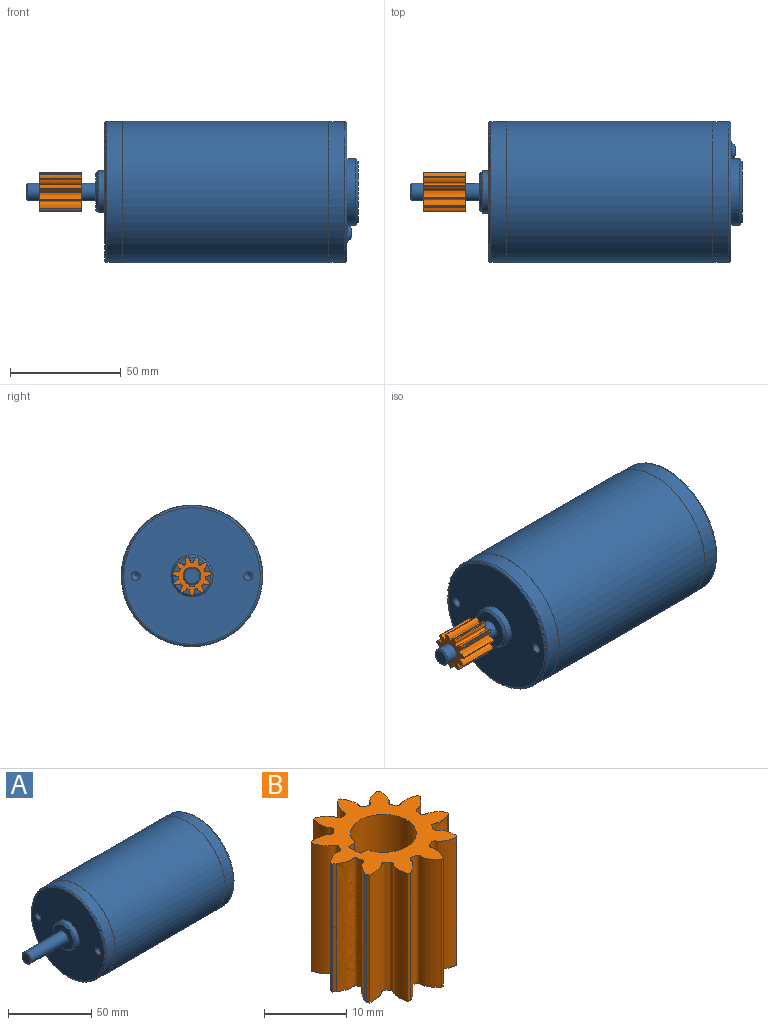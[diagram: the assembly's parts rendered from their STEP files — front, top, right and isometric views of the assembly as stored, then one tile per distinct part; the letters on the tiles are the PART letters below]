
ASSEMBLY  parts=2 mates=1
PART A: 33 faces, bbox 150.2x69x69 mm
  f0: cone r=4mm half-angle=45deg, axis (1,0,0), area 16.7mm2, adj f18,f22
  f1: cone r=9.53mm half-angle=45deg, axis (1,0,0), area 81.4mm2, adj f13,f27
  f2: cone r=14.02mm half-angle=45deg, axis (-1,0,0), area 131.2mm2, adj f17,f23
  f3: cone r=2.12mm half-angle=45deg, axis (-1,0,0), area 62.9mm2, adj f5,f29
  f4: cone r=2.12mm half-angle=45deg, axis (-1,0,0), area 62.9mm2, adj f6,f28
  f5: cylinder r=4.32mm len=8.64mm, axis (-1,0,0), area 1.3mm2, adj f3,f21
  f6: cylinder r=4.32mm len=8.64mm, axis (-1,0,0), area 1.3mm2, adj f4,f21
  f7: cone r=2.02mm half-angle=59deg, axis (-1,0,0), area 14.9mm2, adj f8
  f8: cylinder r=2.02mm len=13.61mm, axis (-1,0,0), area 172.7mm2, adj f7,f26
  f9: cone r=2.02mm half-angle=59deg, axis (-1,0,0), area 14.9mm2, adj f10
  f10: cylinder r=2.02mm len=13.61mm, axis (-1,0,0), area 172.7mm2, adj f9,f26
  f11: torus R=30.88mm, axis (1,0,0), area 311mm2, adj f16,f21
  f12: torus R=30.88mm, axis (-1,0,0), area 311mm2, adj f14,f26
  f13: cylinder r=9.53mm len=19.05mm, axis (1,0,0), area 178.6mm2, adj f1,f26
  f14: cylinder r=31.88mm len=63.75mm, axis (1,0,0), area 1448mm2, adj f12,f25
  f15: cylinder r=32mm len=93.14mm, axis (1,0,0), area 18729.4mm2, adj f24,f25
  f16: cylinder r=31.88mm len=63.75mm, axis (1,0,0), area 1448mm2, adj f11,f24
  f17: cylinder r=15.04mm len=30.07mm, axis (1,0,0), area 376.4mm2, adj f2,f21
  f18: cylinder r=4mm len=31.1mm, axis (1,0,0), area 739mm2, adj f0,f19,f20,f27,f31,f32
  f19: cylinder r=1mm len=2mm, axis (0,1,0), area 3.4mm2, adj f18,f30,f31,f32
  f20: cylinder r=1mm len=2mm, axis (0,-1,0), area 3.4mm2, adj f18,f30,f31,f32
  f21: plane 61.75x61.75mm, normal (1,0,0), area 2167.7mm2, adj f5,f6,f11,f17
  f22: plane 7x7mm, normal (-1,0,0), area 38.5mm2, adj f0
  f23: plane 28.04x28.04mm, normal (1,0,0), area 617.6mm2, adj f2
  f24: plane 64.01x64.01mm, normal (1,0,0), area 25.5mm2, adj f15,f16
  f25: plane 64.01x64.01mm, normal (-1,0,0), area 25.5mm2, adj f14,f15
  f26: plane 61.75x61.75mm, normal (-1,0,0), area 2684.5mm2, adj f8,f10,f12,f13
  f27: plane 17.02x17.02mm, normal (-1,0,0), area 177.2mm2, adj f1,f18
  f28: plane 4.24x4.24mm, normal (1,0,0), area 14.1mm2, adj f4
  f29: plane 4.24x4.24mm, normal (1,0,0), area 14.1mm2, adj f3
  f30: plane 21.5x2mm, normal (0,1,0), area 42.1mm2, adj f19,f20,f31,f32
  f31: plane 19.5x1.07mm, normal (0,0,1), area 20.9mm2, adj f18,f19,f20,f30
  f32: plane 19.5x1.07mm, normal (0,0,-1), area 20.9mm2, adj f18,f19,f20,f30
PART B: 34 faces, bbox 17.6x17.7x19.1 mm
  f0: cylinder r=4mm len=19.05mm, axis (0,0,1), area 439.9mm2, adj f17,f19,f31,f32
  f1: bspline ~9.53x0.35mm, area 4.2mm2, adj f6,f11,f17,f25
  f2: bspline ~9.53x0.41mm, area 4.2mm2, adj f3,f16,f17,f21
  f3: bspline ~9.53x0.41mm, area 4.2mm2, adj f2,f16,f19,f21
  f4: bspline ~19.05x0.44mm, area 8.3mm2, adj f15,f17,f19,f21
  f5: bspline ~19.05x0.41mm, area 8.3mm2, adj f12,f17,f19,f25
  f6: bspline ~9.53x0.35mm, area 4.2mm2, adj f1,f11,f19,f25
  f7: cylinder r=8.94mm len=19.05mm, axis (0,0,1), area 7.5mm2, adj f17,f19,f29,f30
  f8: cylinder r=8.94mm len=19.05mm, axis (0,0,1), area 7.5mm2, adj f17,f19,f28,f29
  f9: cylinder r=8.94mm len=19.05mm, axis (0,0,1), area 7.5mm2, adj f17,f19,f27,f28
  f10: cylinder r=8.94mm len=19.05mm, axis (0,0,1), area 7.5mm2, adj f17,f19,f26,f27
  f11: cylinder r=8.94mm len=19.05mm, axis (0,0,1), area 7.5mm2, adj f1,f6,f17,f19,f26
  f12: cylinder r=8.94mm len=19.05mm, axis (0,0,1), area 7.5mm2, adj f5,f17,f19,f24
  f13: cylinder r=8.94mm len=19.05mm, axis (0,0,1), area 7.5mm2, adj f17,f19,f23,f24
  f14: cylinder r=8.94mm len=19.05mm, axis (0,0,1), area 7.5mm2, adj f17,f19,f22,f23
  f15: cylinder r=8.94mm len=19.05mm, axis (0,0,1), area 7.5mm2, adj f4,f17,f19,f22
  f16: cylinder r=8.94mm len=19.05mm, axis (0,0,1), area 7.5mm2, adj f2,f3,f17,f19,f20
  f17: plane 17.74x17.57mm, normal (0,0,1), area 121.8mm2, adj f0,f1,f2,f4,f5,f7,f8,f9
  f18: cylinder r=8.94mm len=19.05mm, axis (0,0,1), area 7.5mm2, adj f17,f19,f20,f30
  f19: plane 17.74x17.57mm, normal (0,0,-1), area 121.8mm2, adj f0,f3,f4,f5,f6,f7,f8,f9
  f20: bspline ~19.05x4.65mm, area 140.4mm2, adj f16,f17,f18,f19
  f21: bspline ~19.05x3.33mm, area 123.7mm2, adj f2,f3,f4,f17,f19
  f22: bspline ~19.05x4.23mm, area 140.4mm2, adj f14,f15,f17,f19
  f23: bspline ~19.05x4.61mm, area 140.4mm2, adj f13,f14,f17,f19
  f24: bspline ~19.05x3.78mm, area 140.4mm2, adj f12,f13,f17,f19
  f25: bspline ~19.05x3.79mm, area 123.7mm2, adj f1,f5,f6,f17,f19
  f26: bspline ~19.05x4.47mm, area 140.4mm2, adj f10,f11,f17,f19
  f27: bspline ~19.05x3.78mm, area 140.4mm2, adj f9,f10,f17,f19
  f28: bspline ~19.05x4.61mm, area 140.4mm2, adj f8,f9,f17,f19
  f29: bspline ~19.05x4.23mm, area 140.4mm2, adj f7,f8,f17,f19
  f30: bspline ~19.05x3.92mm, area 140.4mm2, adj f7,f17,f18,f19
  f31: plane 19.05x1.13mm, normal (0,-1,0), area 21.5mm2, adj f0,f17,f19,f33
  f32: plane 19.05x1.13mm, normal (0,1,0), area 21.5mm2, adj f0,f17,f19,f33
  f33: plane 19.05x2.02mm, normal (1,0,0), area 38.5mm2, adj f17,f19,f31,f32
PLACE A t=(-37.34,-1.25,-3.74)mm
PLACE B rot(axis=(0,-1,0),90deg) t=(-57.22,-1.25,-3.74)mm
MATE fastened B.f0 <-> A.f0  axis (1,0,0) through (-47.69,-1.25,-3.74)mm
